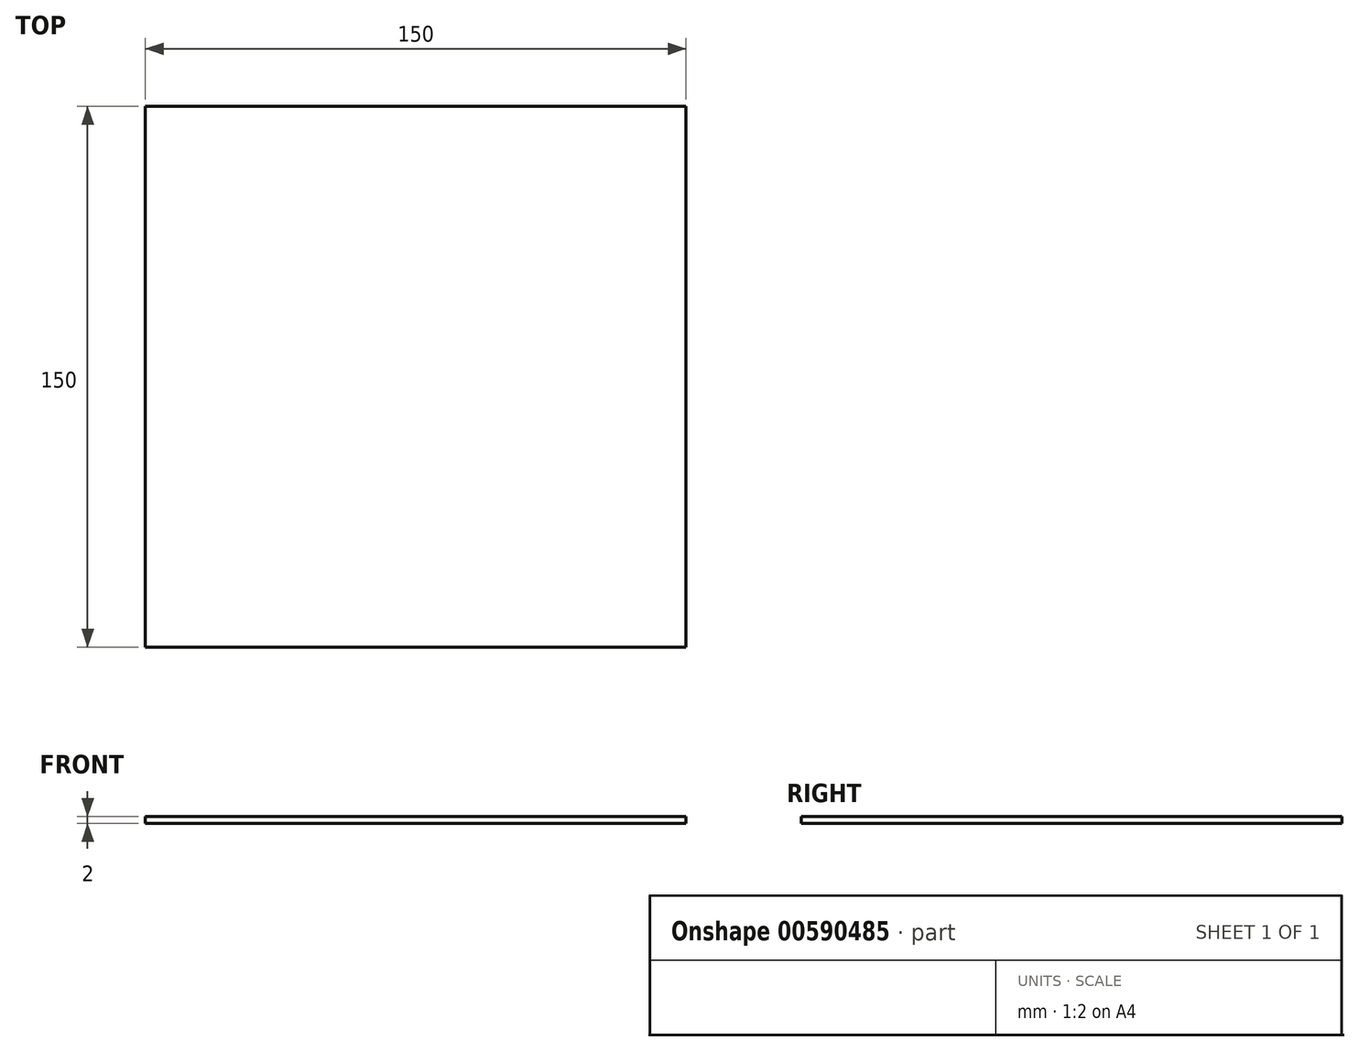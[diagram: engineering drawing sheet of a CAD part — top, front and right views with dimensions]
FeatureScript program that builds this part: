
annotation { "Feature Type Name" : "Feature", "Feature Type Description" : "" }
export const myFeature = defineFeature(function(context is Context, id is Id, definition is map)
    precondition{}
    {
        {
            var Q0;
            Q0=qCreatedBy(makeId("Top.planeOp"),FACE);
            var sketch = newSketch(context, id + "F0", { "sketchPlane" : qUnion([Q0])});
            skLineSegment(sketch, "E0.bottom", {"start": v(75, -75) * mm, "end": v(-75, -75) * mm});
            skLineSegment(sketch, "E0.top", {"start": v(75, 75) * mm, "end": v(-75, 75) * mm});
            skLineSegment(sketch, "E0.left", {"start": v(75, -75) * mm, "end": v(75, 75) * mm});
            skLineSegment(sketch, "E0.right", {"start": v(-75, -75) * mm, "end": v(-75, 75) * mm});
            skPoint(sketch, "E0.middle", {"position": v(0, 0) * mm});
            skSolve(sketch);
        }
        {
            var Q0;
            Q0=makeQuery(id+"F0.imprint","IMPRINT",FACE,{"disambiguationData":[TD([[makeQuery(id+"F0.imprint","IMPRINT",EDGE,{"derivedFrom":sQuery(id+"F0.wireOp",EDGE,"E0.bottom")}),-1.0]])]});
            extrude(context, id + "F1", {"entities" : qUnion([Q0]), "depth" : 2 * mm, "offsetDistance" : 25 * mm});
        }
        {
            var Q0;
            Q0=makeQuery(id+"F1.opExtrude","CAP_FACE",FACE,{"disambiguationData":[OSD([sQuery(id+"F0.wireOp",EDGE,"E0.bottom"),sQuery(id+"F0.wireOp",EDGE,"E0.top"),sQuery(id+"F0.wireOp",EDGE,"E0.left"),sQuery(id+"F0.wireOp",EDGE,"E0.right")])],"isStart":false});
            var sketch = newSketch(context, id + "F2", { "sketchPlane" : qUnion([Q0])});
            skSolve(sketch);
        }
        {
            var Q0;
            Q0=makeQuery(id+"F2.imprint","IMPRINT",FACE,{"disambiguationData":[TD([[makeQuery(id+"F2.imprint","IMPRINT",EDGE,{"derivedFrom":makeQuery(id+"F1.opExtrude","CAP_EDGE",EDGE,{"disambiguationData":[OSD([sQuery(id+"F0.wireOp",EDGE,"E0.bottom")])],"isStart":false})}),-1.0]])]});
            var sketch = newSketch(context, id + "F3", { "sketchPlane" : qUnion([Q0])});
            skLineSegment(sketch, "E1.bottom", {"start": v(74, -74) * mm, "end": v(-74, -74) * mm});
            skLineSegment(sketch, "E1.top", {"start": v(74, 74) * mm, "end": v(-74, 74) * mm});
            skLineSegment(sketch, "E1.left", {"start": v(74, -74) * mm, "end": v(74, 74) * mm});
            skLineSegment(sketch, "E1.right", {"start": v(-74, -74) * mm, "end": v(-74, 74) * mm});
            skPoint(sketch, "E1.middle", {"position": v(0, 0) * mm});
            skSolve(sketch);
        }
        {
            var Q0;
            Q0=makeQuery(id+"F2.imprint","IMPRINT",FACE,{"disambiguationData":[TD([[makeQuery(id+"F2.imprint","IMPRINT",EDGE,{"derivedFrom":makeQuery(id+"F1.opExtrude","CAP_EDGE",EDGE,{"disambiguationData":[OSD([sQuery(id+"F0.wireOp",EDGE,"E0.bottom")])],"isStart":false})}),-1.0]])]});
            var sketch = newSketch(context, id + "F4", { "sketchPlane" : qUnion([Q0])});
            skLineSegment(sketch, "E2.bottom", {"start": v(-73, -73) * mm, "end": v(73, -73) * mm});
            skLineSegment(sketch, "E2.top", {"start": v(-73, 73) * mm, "end": v(73, 73) * mm});
            skLineSegment(sketch, "E2.left", {"start": v(-73, -73) * mm, "end": v(-73, 73) * mm});
            skLineSegment(sketch, "E2.right", {"start": v(73, -73) * mm, "end": v(73, 73) * mm});
            skPoint(sketch, "E2.middle", {"position": v(0, 0) * mm});
            skSolve(sketch);
        }
        {
            var Q0;
            Q0=sQuery(id+"F3.wireOp",EDGE,"E1.top");
            var Q1;
            Q1=sQuery(id+"F4.wireOp",EDGE,"E2.top");
            var Q2;
            Q2=sQuery(id+"F4.wireOp",EDGE,"E2.right");
            var Q3;
            Q3=sQuery(id+"F3.wireOp",EDGE,"E1.left");
            var Q4;
            Q4=sQuery(id+"F4.wireOp",EDGE,"E2.left");
            var Q5;
            Q5=sQuery(id+"F3.wireOp",EDGE,"E1.right");
            var Q6;
            Q6=sQuery(id+"F4.wireOp",EDGE,"E2.bottom");
            var Q7;
            Q7=sQuery(id+"F3.wireOp",EDGE,"E1.bottom");
            extrude(context, id + "F5", {"bodyType" : ToolBodyType.SURFACE, "surfaceEntities" : qUnion([Q0, Q1, Q2, Q3, Q4, Q5, Q6, Q7]), "depth" : 25 * mm, "offsetDistance" : 25 * mm});
        }
    });
